MODEL slx_f9ed8deba307
KIND model
CONFIG AbsTol = auto
CONFIG FixedStep = auto
CONFIG MaxStep = auto
CONFIG MinStep = auto
CONFIG RelTol = 1e-3
CONFIG SampleTimeConstraint = Unconstrained
CONFIG Solver = FixedStepAuto
CONFIG SolverMode = SingleTasking
CONFIG SolverName = FixedStepAuto
CONFIG StartTime = 0.0
CONFIG StopTime = inf
BLOCK [S-Function] Coppelia Sim Open//Play//Stop
  EnableBusSupport = off
  FunctionName = vrepCommand
  Parameters = scene
  Ports = []
  SFunctionDeploymentMode = off
BLOCK [Demux] Demux
  DisplayOption = bar
  Outputs = 3
  Ports = [1, 3]
BLOCK [Display] Display
  Decimation = 1
  Ports = [1]
BLOCK [Display] Display1
  Decimation = 1
  Ports = [1]
BLOCK [Display] Display2
  Decimation = 1
  Ports = [1]
BLOCK [SubSystem] Gauge
  DialogController = hmiCreateDDGDialog
  IsWebBlock = on
  Ports = []
  RequestExecContextInheritance = off
BLOCK [Constant] Left Wheel Speed
  Value = 2.8
BLOCK [Mux] Mux
  DisplayOption = bar
  Inputs = 2
  Ports = [2, 1]
BLOCK [Constant] Rigth wheel Speed
  Value = 4.152892561983471
BLOCK [Reference] Simulation Pace  REF=aerolibanimutils/Simulation Pace
  AttributesFormatString = %<SleepMode>\n%<SimulationPace> sec/sec
  Ports = []
  SourceBlock = aerolibanimutils/Simulation Pace
  SourceType = Simulation Pace
BLOCK [SubSystem] Slider
  DialogController = hmiCreateDDGDialog
  IsWebBlock = on
  Ports = []
  RequestExecContextInheritance = off
BLOCK [SubSystem] Slider1
  DialogController = hmiCreateDDGDialog
  IsWebBlock = on
  Ports = []
  RequestExecContextInheritance = off
BLOCK [S-Function] getTable
  EnableBusSupport = off
  FunctionName = gettable
  Parameters = tname
  Ports = [0, 1]
  SFunctionDeploymentMode = off
BLOCK [S-Function] setTable
  EnableBusSupport = off
  FunctionName = settable
  Parameters = tname
  Ports = [1]
  SFunctionDeploymentMode = off
ANNOTATION (root): CoppeliaSim Simulink Communication plugin. Version beta 1.2 Author : Dr. Ing. Diego Daniel Santiago. <email> <email> Facultad de Ingeniería Universidad Nacional de San Juan San Juan - Argentina INAUT - Instituto de Automática http://www.inaut.unsj.edu.ar/ CONICET - Consejo Nacional de Investigaciones Científicas y Técnicas. http://www.conicet.gov.ar/
LINE Demux:1 -> Display:1
LINE Demux:2 -> Display1:1
LINE Demux:3 -> Display2:1
LINE Left Wheel Speed:1 -> Mux:1
LINE Mux:1 -> setTable:1
LINE Rigth wheel Speed:1 -> Mux:2
LINE getTable:1 -> Demux:1
